# Revit family: Plumbing Fixture-Grease_Interseptor_Mifab_MI-SOLID -TA
name_source: partatom
category: Plumbing Fixtures
revit_build: Autodesk Revit Structure 2013 (Build: 20120221_2030(x64)
units: mm (PartAtom-declared; Revit-internal decimal feet)

## types (9) — shared parameters
Assembly Code = D2090300
Default Elevation = 0"
Description = Top Access Solids Interceptor
H = 9 7/8"
Interceptor Material = Acid Resistant Epoxy Coated Black
Manufacturer = MIFAB
URL = www.mifab.com
zero-valued in all types: WFU

## per-type parameters (varying)
| type | A | B | D | Flow Rate | Grease Capacity | I | Pipe Size | Standard Inlet And Outlet Radii |
| MI-SOLID-TA-0 | 10" | 9 7/8" | 7 1/4" | 4 GPM | 23 lbs | 11" | 2" | 1" |
| MI-SOLID-TA-1 | 11 1/8" | 11 7/8" | 8 1/8" | 7 GPM | 30 lbs | 13" | 2" | 1" |
| MI-SOLID-TA-2 | 11 3/4" | 14" | 8 1/4" | 10 GPM | 40 lbs | 15 1/8" | 3" | 1 1/2" |
| MI-SOLID-TA-3 | 13 3/8" | 16 3/4" | 9 3/8" | 15 GPM | 50 lbs | 17 7/8" | 3" | 1 1/2" |
| MI-SOLID-TA-4 | 15" | 17 1/4" | 11 3/4" | 20 GPM | 60 lbs | 18 3/8" | 3" | 1 1/2" |
| MI-SOLID-TA-5 | 17" | 19 7/8" | 12 1/2" | 25 GPM | 80 lbs | 21" | 4" | 2" |
| MI-SOLID-TA-6 | 18 3/4" | 22 1/2" | 14 1/4" | 35 GPM | 90 lbs | 23 5/8" | 4" | 2" |
| MI-SOLID-TA-7 | 21 1/2" | 22 1/2" | 16" | 50 GPM | 100 lbs | 23 5/8" | 4" | 2" |
| MI-SOLID-TA-8 | 22 3/4" | 22 1/2" | 18 1/2" | 75 GPM | 110 lbs | 23 5/8" | 4" | 2" |

note: column(s) folded — value = type name in every type: Model

## geometry (parser evidence)
native form markers: Blend x4, Sweep x1
no freeform markers — native parametric forms only
